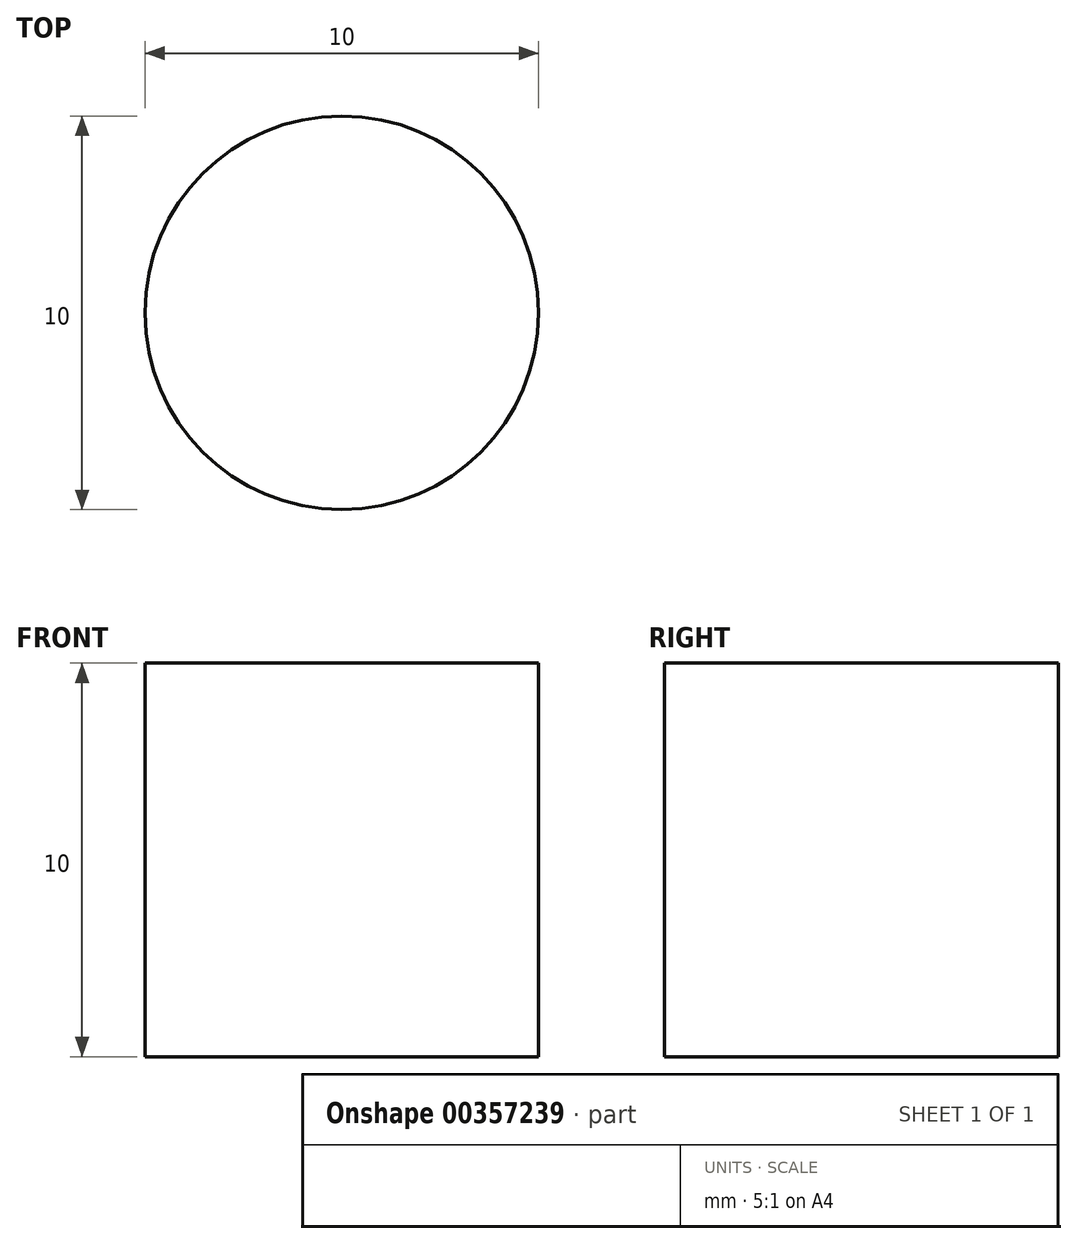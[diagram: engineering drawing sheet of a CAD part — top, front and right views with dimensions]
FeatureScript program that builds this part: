
annotation { "Feature Type Name" : "Feature", "Feature Type Description" : "" }
export const myFeature = defineFeature(function(context is Context, id is Id, definition is map)
    precondition{}
    {
        {
            var Q0;
            Q0=qCreatedBy(makeId("Top.planeOp"),FACE);
            var sketch = newSketch(context, id + "F0", { "sketchPlane" : qUnion([Q0])});
            skCircle(sketch, "E0", {"center": v(0, 0) * mm, "radius": 5 * mm});
            skSolve(sketch);
        }
        {
            var Q0;
            Q0 = qSketchRegion(id + "F0", true);
            extrude(context, id + "F1", {"entities" : qUnion([Q0]), "depth" : 10 * mm});
        }
    });
